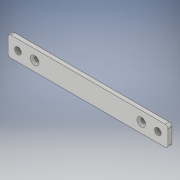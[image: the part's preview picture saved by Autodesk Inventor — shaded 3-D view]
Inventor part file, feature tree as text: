
AUTODESK INVENTOR PART (.ipt)
format: ipt  version: 2019 (Build 230136000, 136)  size: 119,296 bytes
history: native  units: mm
features: sketch x2, extrude x1, hole x1, fillet x1
ambient origin geometry x8: Origin, YZ Plane, XZ Plane, XY Plane, X Axis, Y Axis, Z Axis, Center Point
bodies: Solid1 (feature_tree)
feature tree (5):
  extrude  "Extrusion1"  Depth=15.0mm
  hole  "Hole1"  [1 undecoded]
  fillet  "Fillet1"  Radius=7.5mm
  sketch  "Sketch1"  dims[d0=120.0mm d1=15.0mm]
  sketch  "Sketch2"  dims[d2=5.0mm d3=7.5mm d4=7.5mm d5=3.0mm d6=0.0mm d7=80.0mm d8=3.3mm d9=6.0mm d10=6.5mm d11=2.0mm d12=90.0deg d13=36.25mm d14=0.0mm d15=2.0mm]
note: 1 required parameter value undecoded (feature->parameter linkage not recoverable at this tier; creation-order binding heuristic only, values carry confidence <= 0.55)
